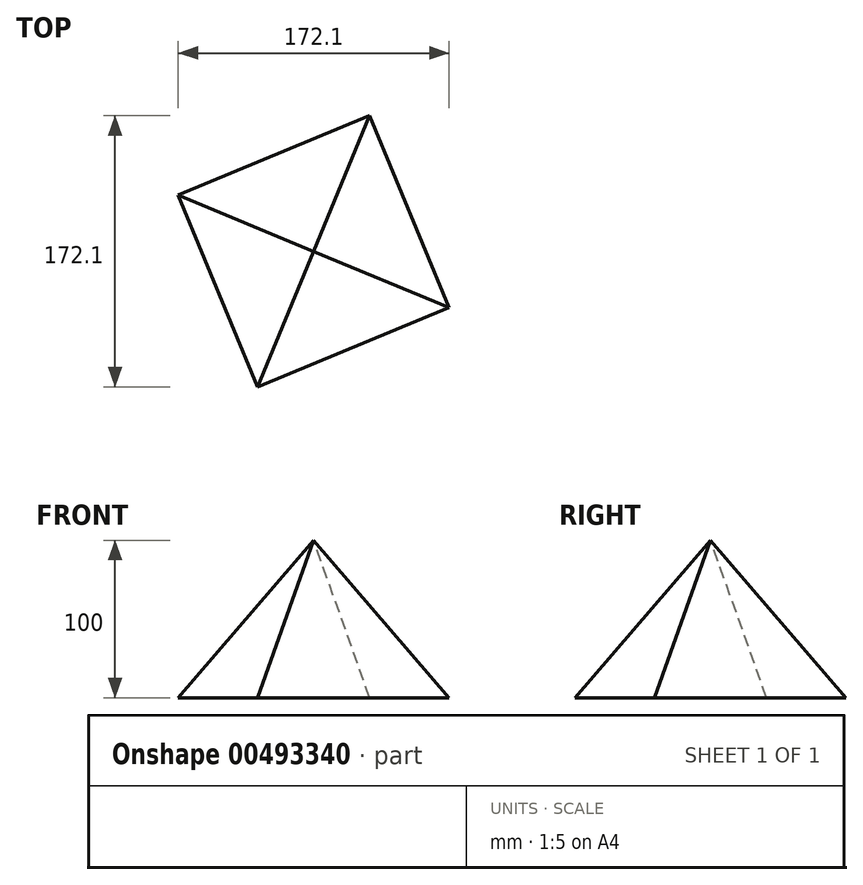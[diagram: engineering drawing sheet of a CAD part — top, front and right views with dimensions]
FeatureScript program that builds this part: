
annotation { "Feature Type Name" : "Feature", "Feature Type Description" : "" }
export const myFeature = defineFeature(function(context is Context, id is Id, definition is map)
    precondition{}
    {
        {
            var Q0;
            Q0=qCreatedBy(makeId("Top.planeOp"),FACE);
            var sketch = newSketch(context, id + "F0", { "sketchPlane" : qUnion([Q0])});
            skCircle(sketch, "E0.cCircle", {"center": v(0, 0) * mm, "radius": 93.12 * mm, "construction": true});
            skLineSegment(sketch, "E0.0", {"start": v(-86.05, 35.6) * mm, "end": v(35.6, 86.05) * mm});
            skLineSegment(sketch, "E0.1", {"start": v(35.6, 86.05) * mm, "end": v(86.05, -35.6) * mm});
            skLineSegment(sketch, "E0.2", {"start": v(86.05, -35.6) * mm, "end": v(-35.6, -86.05) * mm});
            skLineSegment(sketch, "E0.3", {"start": v(-35.6, -86.05) * mm, "end": v(-86.05, 35.6) * mm});
            skSolve(sketch);
        }
        {
            var Q0;
            Q0=qCreatedBy(makeId("Top.planeOp"),FACE);
            cPlane(context, id + "F1", {"entities" : qUnion([Q0]), "cplaneType" : CPlaneType.OFFSET, "offset" : 100 * mm, "width" : 150 * mm, "height" : 150 * mm});
        }
        {
            var Q0;
            Q0=qCreatedBy(id+"F1.planeOp",FACE);
            var sketch = newSketch(context, id + "F2", { "sketchPlane" : qUnion([Q0])});
            skPoint(sketch, "E1", {"position": v(0, 0) * mm});
            skSolve(sketch);
        }
        {
            var Q0;
            Q0=makeQuery(id+"F0.imprint","IMPRINT",FACE,{"disambiguationData":[TD([[makeQuery(id+"F0.imprint","IMPRINT",EDGE,{"derivedFrom":sQuery(id+"F0.wireOp",EDGE,"E0.0")}),-1.0]])]});
            var Q1;
            Q1=sQuery(id+"F2.wireOp",VERTEX,"E1");
            loft(context, id + "F3", {"sheetProfilesArray" : [{ "sheetProfileEntities" : qUnion([Q0]) }, { "sheetProfileEntities" : qUnion([Q1]) }]});
        }
    });
